# Revit family: B-820-02
name_source: partatom
category: Equipement spécialisé
units: mm (PartAtom-declared; Revit-internal decimal feet)

## family parameters
Autoriser la découpe dans les vues = Non
Basée sur le plan de construction = Oui
Conserver l'orientation des annotations = Non
Cote de connecteur circulaire = Utiliser le diamètre
Couper avec des vides une fois chargée = Non
Numéro OmniClass = 23.40.20.21.34
Partagée = Oui
Repère de localisation dans la pièce = Non
Titre OmniClass = Soap Holders, Dispensers
Toujours verticalement = Non
Type d'élément = Normal

## types (2) — shared parameters
6V AC Adapter 3974-58 = Non
6V AC Adapter 824-241 = Non
B-820 (Multi-Feed Soap Reservoir Tank) = Oui
Capacity = 1.6 gal (6.0 L)
Code d'assemblage = C1030200
Contertop Thickness = 1"
Contertop Thickness Constraint = 1"
Description = AUTOMATIC, TOP-FILL, MULTI-FEED BULK SOAP DISPENSER SYSTEM
Dispenser 1 = Oui
Dispenser 2 = Oui
Dispenser 3 = Oui
Dispenser 4 = Oui
Dispenser 5 = Oui
Dispenser 6 = Oui
Distance between Dispensers = 43 5/16"
Distance between Dispensers Constraint = 43 5/16"
Elévation par défaut = 0"
Fabricant = Bobrick
Height = 3 29/32"
Installation Type = Deck Mounted
Material = Stainkess Steel-Bobrick-Polished
Min. Clearanace to back of Wall = 1 3/8"
Soap Reservoir Tank Material = Polypropylene-Bobrick-Black
Spout and Stem Assembly Material = Stainkess Steel-Bobrick-Polished
Tube Length = 6"
Tube Length Constraint = 6"
Width = 1 11/16"

## per-type parameters (varying)
| type | Commentaires du type | Nom du vendeur / Seller's name | Type of Dispenser | URL |
| B-820-258 | Liquid Soap Pump |  | B-820 : B-820-258 | https://www.bobrick.com |
| B-820-248 | Foam Soap Pump | ANOX Diffusion | B-820 : B-820-248 | https://www.anox.fr |

note: column(s) folded — value = type name in every type: Modèle

## geometry (parser evidence)
native form markers: Sweep x6
no freeform markers — native parametric forms only
